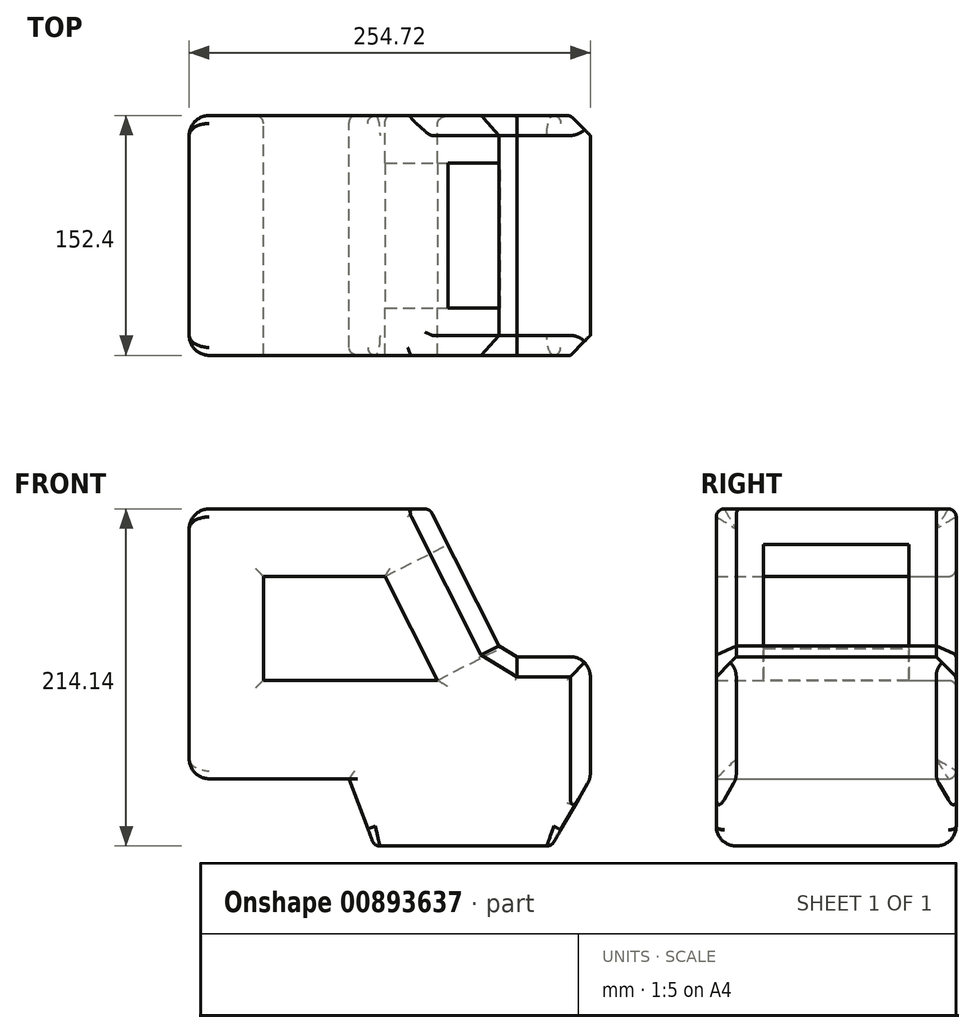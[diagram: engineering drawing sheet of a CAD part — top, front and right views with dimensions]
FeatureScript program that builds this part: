
annotation { "Feature Type Name" : "Feature", "Feature Type Description" : "" }
export const myFeature = defineFeature(function(context is Context, id is Id, definition is map)
    precondition{}
    {
        {
            var Q0;
            Q0=qCreatedBy(makeId("Front.planeOp"),FACE);
            var sketch = newSketch(context, id + "F0", { "sketchPlane" : qUnion([Q0])});
            skLineSegment(sketch, "E0", {"start": v(-101.6, 171.45) * mm, "end": v(51.16, 171.45) * mm});
            skLineSegment(sketch, "E1", {"start": v(51.16, 171.45) * mm, "end": v(98.68, 77.56) * mm});
            skLineSegment(sketch, "E2", {"start": v(98.68, 77.56) * mm, "end": v(153.12, 77.56) * mm});
            skLineSegment(sketch, "E3", {"start": v(153.12, 77.56) * mm, "end": v(153.12, 0) * mm});
            skLineSegment(sketch, "E4", {"start": v(153.12, 0) * mm, "end": v(0, 0) * mm});
            skLineSegment(sketch, "E5", {"start": v(0, 0) * mm, "end": v(0, 0) * mm});
            skLineSegment(sketch, "E6", {"start": v(0, 0) * mm, "end": v(-101.6, 0) * mm});
            skLineSegment(sketch, "E7", {"start": v(-101.6, 0) * mm, "end": v(-101.6, 171.45) * mm});
            skLineSegment(sketch, "E8", {"start": v(22.77, 128.51) * mm, "end": v(56.1, 62.66) * mm});
            skLineSegment(sketch, "E9", {"start": v(-54.5, 62.66) * mm, "end": v(-54.5, 128.51) * mm});
            skLineSegment(sketch, "E10", {"start": v(-54.5, 128.51) * mm, "end": v(22.77, 128.51) * mm});
            skLineSegment(sketch, "E11", {"start": v(-54.5, 62.66) * mm, "end": v(56.1, 62.66) * mm});
            skLineSegment(sketch, "E12", {"start": v(0, 0) * mm, "end": v(15.9, -42.7) * mm});
            skLineSegment(sketch, "E13", {"start": v(15.9, -42.7) * mm, "end": v(128.45, -42.7) * mm});
            skLineSegment(sketch, "E14", {"start": v(128.45, -42.7) * mm, "end": v(153.12, 0) * mm});
            skSolve(sketch);
        }
        {
            var Q0;
            Q0=makeQuery(id+"F0.imprint","IMPRINT",FACE,{"disambiguationData":[TD([[makeQuery(id+"F0.imprint","IMPRINT",EDGE,{"derivedFrom":sQuery(id+"F0.wireOp",EDGE,"E0")}),-1.0]])]});
            var Q1;
            Q1=makeQuery(id+"F0.imprint","IMPRINT",FACE,{"disambiguationData":[TD([[makeQuery(id+"F0.imprint","IMPRINT",EDGE,{"derivedFrom":sQuery(id+"F0.wireOp",EDGE,"E4")}),1.0]])]});
            extrude(context, id + "F1", {"entities" : qUnion([Q0, Q1]), "endBound" : BoundingType.SYMMETRIC, "depth" : 152.4 * mm, "offsetDistance" : 25.4 * mm});
        }
        {
            var Q0;
            Q0=makeQuery(id+"F1.opExtrude","CAP_EDGE",EDGE,{"disambiguationData":[OSD([sQuery(id+"F0.wireOp",EDGE,"E2")])],"isStart":false});
            var Q1;
            Q1=makeQuery(id+"F1.opExtrude","CAP_EDGE",EDGE,{"disambiguationData":[OSD([sQuery(id+"F0.wireOp",EDGE,"E2")])],"isStart":true});
            var Q2;
            Q2=makeQuery(id+"F1.opExtrude","CAP_EDGE",EDGE,{"disambiguationData":[OSD([sQuery(id+"F0.wireOp",EDGE,"E3")])],"isStart":false});
            var Q3;
            Q3=makeQuery(id+"F1.opExtrude","CAP_EDGE",EDGE,{"disambiguationData":[OSD([sQuery(id+"F0.wireOp",EDGE,"E3")])],"isStart":true});
            var Q4;
            Q4=makeQuery(id+"F1.opExtrude","SWEPT_EDGE",EDGE,{"disambiguationData":[OSD([sQuery(id+"F0.wireOp",EDGE,"E1"),sQuery(id+"F0.wireOp",EDGE,"E2")])]});
            chamfer(context, id + "F2", {"entities" : qUnion([Q0, Q1, Q2, Q3, Q4]), "width" : 12.7 * mm, "tangentPropagation" : true});
        }
        {
            var Q0;
            Q0=makeQuery(id+"F1.opExtrude","SWEPT_EDGE",EDGE,{"disambiguationData":[OSD([sQuery(id+"F0.wireOp",EDGE,"E2"),sQuery(id+"F0.wireOp",EDGE,"E3")])]});
            fillet(context, id + "F3", {"entities" : qUnion([Q0]), "radius" : 12.7 * mm, "tangentPropagation" : true, "allowEdgeOverflow" : false});
        }
        {
            var Q0;
            Q0=makeQuery(id+"F1.opExtrude","SWEPT_FACE",FACE,{"disambiguationData":[OSD([sQuery(id+"F0.wireOp",EDGE,"E1")])]});
            cPlane(context, id + "F4", {"entities" : qUnion([Q0]), "cplaneType" : CPlaneType.OFFSET, "offset" : 0 * mm, "width" : 152.4 * mm, "height" : 152.4 * mm});
        }
        {
            var Q0;
            Q0=qCreatedBy(id+"F4.planeOp",FACE);
            var sketch = newSketch(context, id + "F5", { "sketchPlane" : qUnion([Q0])});
            skLineSegment(sketch, "E15.0", {"start": v(-76.2, 104.38) * mm, "end": v(76.2, 104.38) * mm});
            skLineSegment(sketch, "E16.0", {"start": v(-76.2, 30.57) * mm, "end": v(76.2, 30.57) * mm});
            skLineSegment(sketch, "E17.bottom", {"start": v(46.09, 30.57) * mm, "end": v(-46.09, 30.57) * mm});
            skLineSegment(sketch, "E17.top", {"start": v(46.09, 104.38) * mm, "end": v(-46.09, 104.38) * mm});
            skLineSegment(sketch, "E17.left", {"start": v(46.09, 30.57) * mm, "end": v(46.09, 104.38) * mm});
            skLineSegment(sketch, "E17.right", {"start": v(-46.09, 30.57) * mm, "end": v(-46.09, 104.38) * mm});
            skPoint(sketch, "E17.middle", {"position": v(0, 67.47) * mm});
            skSolve(sketch);
        }
        {
            var Q0;
            {var subQ2=sQuery(id+"F5.wireOp",EDGE,"E17.left");Q0=makeQuery(id+"F5.imprint","IMPRINT",FACE,{"disambiguationData":[TD([[makeQuery(id+"F5.imprint","IMPRINT",EDGE,{"derivedFrom":subQ2}),1.0]])]});}
            var Q1;
            Q1=makeQuery(id+"F1.opExtrude","SWEPT_FACE",FACE,{"disambiguationData":[OSD([sQuery(id+"F0.wireOp",EDGE,"E8")])]});
            extrude(context, id + "F6", {"entities" : qUnion([Q0]), "operationType" : NewBodyOperationType.REMOVE, "endBound" : BoundingType.UP_TO_SURFACE, "oppositeDirection" : true, "depth" : 25.4 * mm, "endBoundEntityFace" : qUnion([Q1]), "offsetDistance" : 25.4 * mm});
        }
        {
            var Q0;
            Q0=makeQuery(id+"F1.opExtrude","SWEPT_EDGE",EDGE,{"disambiguationData":[OSD([sQuery(id+"F0.wireOp",EDGE,"E0"),sQuery(id+"F0.wireOp",EDGE,"E7")])]});
            var Q1;
            Q1=makeQuery(id+"F1.opExtrude","SWEPT_EDGE",EDGE,{"disambiguationData":[OSD([sQuery(id+"F0.wireOp",EDGE,"E6"),sQuery(id+"F0.wireOp",EDGE,"E7")])]});
            var Q2;
            Q2=makeQuery(id+"F1.opExtrude","CAP_EDGE",EDGE,{"disambiguationData":[OSD([sQuery(id+"F0.wireOp",EDGE,"E7")])],"isStart":true});
            var Q3;
            Q3=makeQuery(id+"F1.opExtrude","CAP_EDGE",EDGE,{"disambiguationData":[OSD([sQuery(id+"F0.wireOp",EDGE,"E7")])],"isStart":false});
            var Q4;
            Q4=makeQuery(id+"F1.opExtrude","CAP_EDGE",EDGE,{"disambiguationData":[OSD([sQuery(id+"F0.wireOp",EDGE,"E13")])],"isStart":false});
            var Q5;
            Q5=makeQuery(id+"F1.opExtrude","CAP_EDGE",EDGE,{"disambiguationData":[OSD([sQuery(id+"F0.wireOp",EDGE,"E13")])],"isStart":true});
            var Q6;
            Q6=makeQuery(id+"F1.opExtrude","SWEPT_EDGE",EDGE,{"disambiguationData":[OSD([sQuery(id+"F0.wireOp",EDGE,"E3"),sQuery(id+"F0.wireOp",EDGE,"E4"),sQuery(id+"F0.wireOp",EDGE,"E14")])]});
            fillet(context, id + "F7", {"entities" : qUnion([Q0, Q1, Q2, Q3, Q4, Q5, Q6]), "radius" : 12.7 * mm, "tangentPropagation" : true, "allowEdgeOverflow" : false});
        }
        {
            var Q0;
            Q0=makeQuery(id+"F1.opExtrude","SWEPT_EDGE",EDGE,{"disambiguationData":[OSD([sQuery(id+"F0.wireOp",EDGE,"E0"),sQuery(id+"F0.wireOp",EDGE,"E1")])]});
            var Q1;
            Q1=makeQuery(id+"F2.opChamfer","BLEND_EDGE",EDGE,{"blendedFrom":[makeQuery(id+"F1.opExtrude","CAP_EDGE",EDGE,{"disambiguationData":[OSD([sQuery(id+"F0.wireOp",EDGE,"E1")])],"isStart":false}),makeQuery(id+"F1.opExtrude","SWEPT_FACE",FACE,{"disambiguationData":[OSD([sQuery(id+"F0.wireOp",EDGE,"E0")])]})],"blendedInto":[makeQuery(id+"F1.opExtrude","SWEPT_FACE",FACE,{"disambiguationData":[OSD([sQuery(id+"F0.wireOp",EDGE,"E0")])]})]});
            var Q2;
            Q2=makeQuery(id+"F1.opExtrude","CAP_EDGE",EDGE,{"disambiguationData":[OSD([sQuery(id+"F0.wireOp",EDGE,"E0")])],"isStart":false});
            var Q3;
            Q3=makeQuery(id+"F1.opExtrude","CAP_FACE",FACE,{"disambiguationData":[OSD([sQuery(id+"F0.wireOp",EDGE,"E0"),sQuery(id+"F0.wireOp",EDGE,"E1"),sQuery(id+"F0.wireOp",EDGE,"E2"),sQuery(id+"F0.wireOp",EDGE,"E3"),sQuery(id+"F0.wireOp",EDGE,"E6"),sQuery(id+"F0.wireOp",EDGE,"E7"),sQuery(id+"F0.wireOp",EDGE,"E8"),sQuery(id+"F0.wireOp",EDGE,"E9"),sQuery(id+"F0.wireOp",EDGE,"E10"),sQuery(id+"F0.wireOp",EDGE,"E11"),sQuery(id+"F0.wireOp",EDGE,"E12"),sQuery(id+"F0.wireOp",EDGE,"E13"),sQuery(id+"F0.wireOp",EDGE,"E14")])],"isStart":true});
            var Q4;
            Q4=makeQuery(id+"F1.opExtrude","CAP_EDGE",EDGE,{"disambiguationData":[OSD([sQuery(id+"F0.wireOp",EDGE,"E0")])],"isStart":true});
            fillet(context, id + "F8", {"entities" : qUnion([Q0, Q1, Q2, Q3, Q4]), "radius" : 5.08 * mm, "tangentPropagation" : true, "allowEdgeOverflow" : false});
        }
    });
